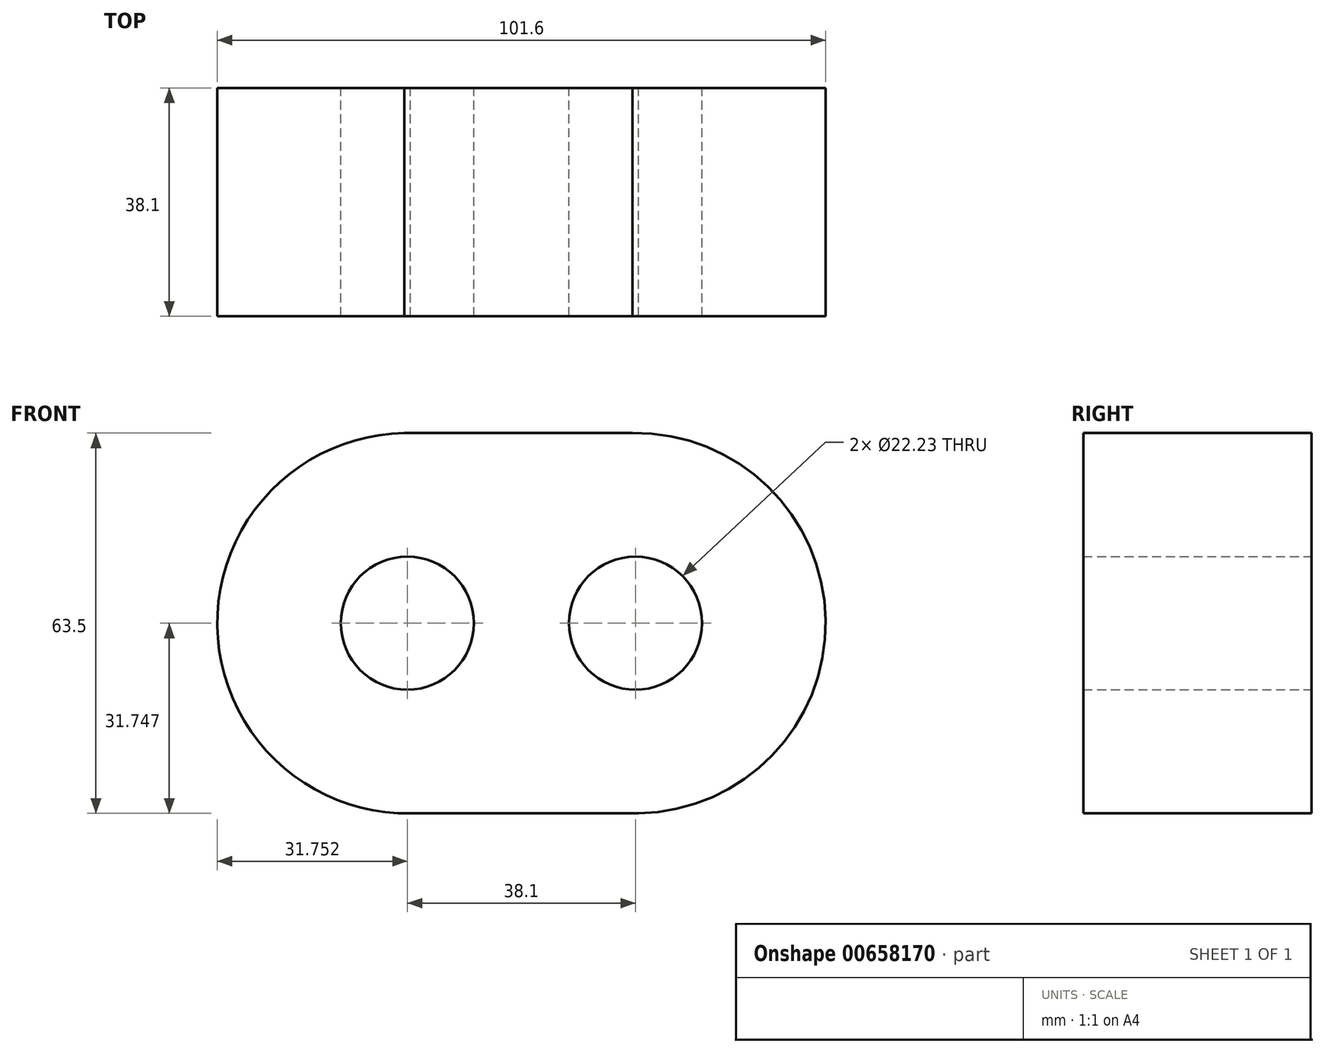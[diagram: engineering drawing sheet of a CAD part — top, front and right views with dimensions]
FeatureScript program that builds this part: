
annotation { "Feature Type Name" : "Feature", "Feature Type Description" : "" }
export const myFeature = defineFeature(function(context is Context, id is Id, definition is map)
    precondition{}
    {
        {
            var Q0;
            Q0=qCreatedBy(makeId("Front.planeOp"),FACE);
            var sketch = newSketch(context, id + "F0", { "sketchPlane" : qUnion([Q0])});
            skPoint(sketch, "E0.endSnap0", {"position": v(-28.74, -43.32) * mm});
            skLineSegment(sketch, "E1", {"start": v(-1, 28.7) * mm, "end": v(-39.1, 28.7) * mm});
            skLineSegment(sketch, "E2", {"start": v(-38.1, -34.79) * mm, "end": v(0, -34.79) * mm});
            skArc(sketch, "E3", {"start": v(0, -34.79) * mm, "mid": v(31.25, -2.54) * mm, "end": v(-1, 28.7) * mm});
            skArc(sketch, "E4", {"start": v(-39.1, 28.7) * mm, "mid": v(-70.34, -3.54) * mm, "end": v(-38.1, -34.79) * mm});
            skCircle(sketch, "E5", {"center": v(-38.6, -3.04) * mm, "radius": 11.11 * mm});
            skCircle(sketch, "E6", {"center": v(-0.5, -3.04) * mm, "radius": 11.11 * mm});
            skSolve(sketch);
        }
        {
            var Q0;
            Q0 = qSketchRegion(id + "F0", true);
            extrude(context, id + "F1", {"entities" : qUnion([Q0]), "depth" : 38.1 * mm, "offsetDistance" : 25.4 * mm});
        }
    });
